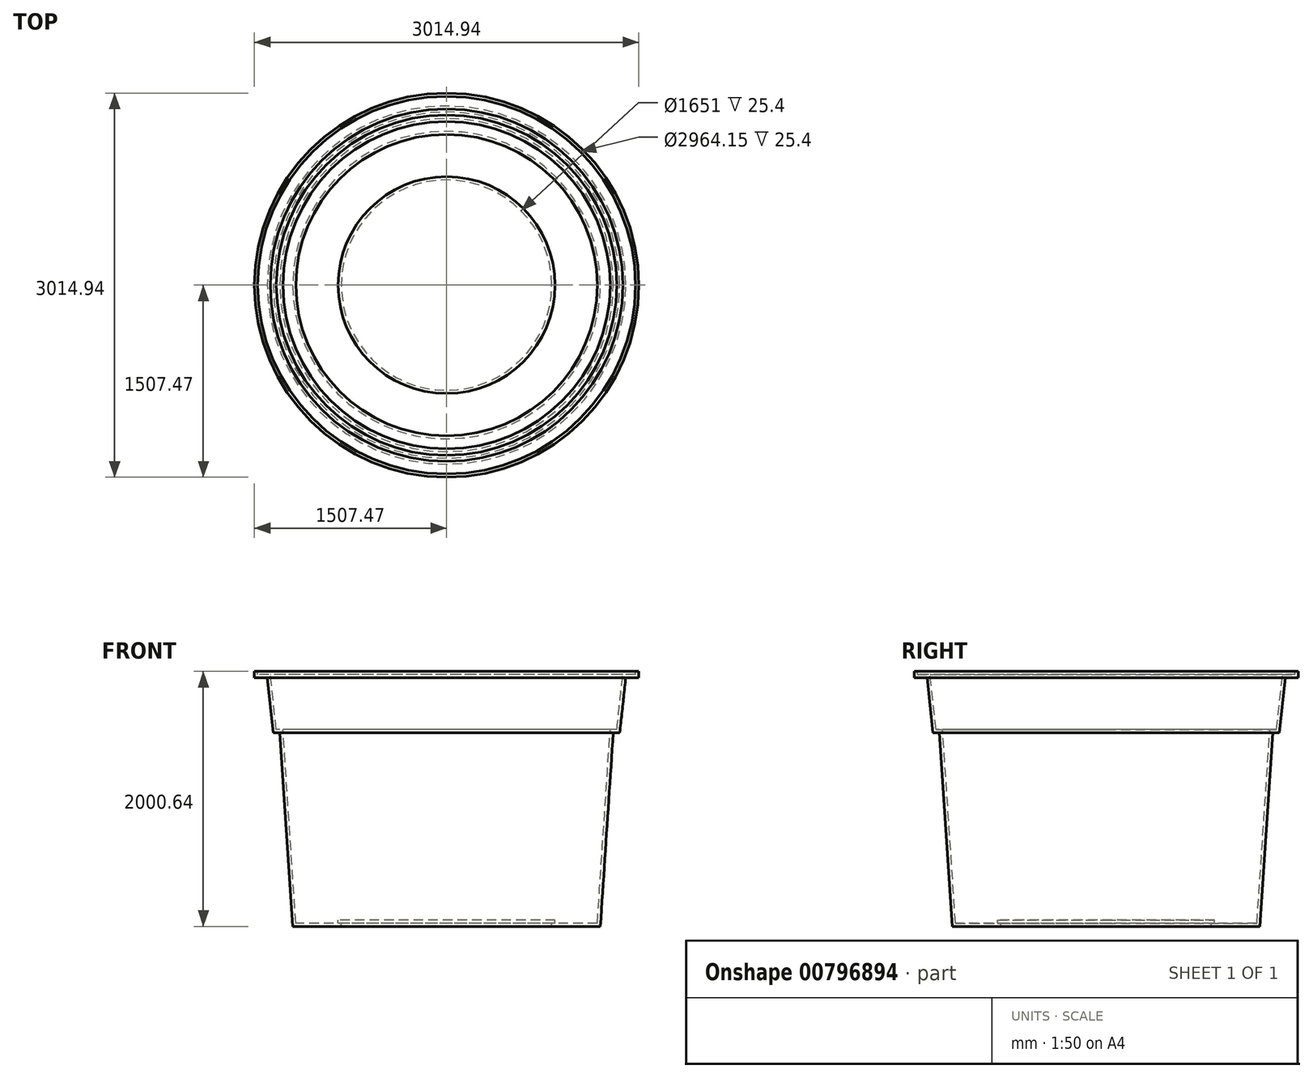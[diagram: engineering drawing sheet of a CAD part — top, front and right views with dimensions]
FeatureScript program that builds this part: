
annotation { "Feature Type Name" : "Feature", "Feature Type Description" : "" }
export const myFeature = defineFeature(function(context is Context, id is Id, definition is map)
    precondition{}
    {
        {
            var Q0;
            Q0=qCreatedBy(makeId("Front.planeOp"),FACE);
            var sketch = newSketch(context, id + "F0", { "sketchPlane" : qUnion([Q0])});
            skLineSegment(sketch, "E0", {"start": v(0, 25.4) * mm, "end": v(-825.5, 25.4) * mm});
            skLineSegment(sketch, "E1", {"start": v(-825.5, 25.4) * mm, "end": v(-825.5, 0) * mm});
            skLineSegment(sketch, "E2", {"start": v(-825.5, 0) * mm, "end": v(-1206.5, 0) * mm});
            skLineSegment(sketch, "E3", {"start": v(-1206.5, 0) * mm, "end": v(-1307.88, 1520.62) * mm});
            skLineSegment(sketch, "E4", {"start": v(-1307.88, 1520.62) * mm, "end": v(-1358.68, 1520.62) * mm});
            skLineSegment(sketch, "E5", {"start": v(-1358.68, 1520.62) * mm, "end": v(-1405.87, 1949.84) * mm});
            skLineSegment(sketch, "E6", {"start": v(-1405.87, 1949.84) * mm, "end": v(-1507.47, 1949.84) * mm});
            skLineSegment(sketch, "E7", {"start": v(-1507.47, 1949.84) * mm, "end": v(-1507.47, 2000.64) * mm});
            skLineSegment(sketch, "E8", {"start": v(-1507.47, 2000.64) * mm, "end": v(0, 2000.64) * mm});
            skLineSegment(sketch, "E9", {"start": v(0, 2000.64) * mm, "end": v(0, 25.4) * mm});
            skSolve(sketch);
        }
        {
            var Q0;
            Q0 = qSketchRegion(id + "F0", true);
            var Q1;
            Q1=sQuery(id+"F0.wireOp",EDGE,"E9");
            revolve(context, id + "F1", {"surfaceOperationType" : NewSurfaceOperationType.NEW, "entities" : qUnion([Q0]), "axis" : qUnion([Q1]), "revolveType" : RevolveType.FULL});
        }
        {
            var Q0;
            Q0=makeQuery(id+"F1.opRevolve","SWEPT_FACE",FACE,{"disambiguationData":[OSD([sQuery(id+"F0.wireOp",EDGE,"E8")])]});
            shell(context, id + "F2", {"entities" : qUnion([Q0]), "thickness" : 25.4 * mm});
        }
    });
